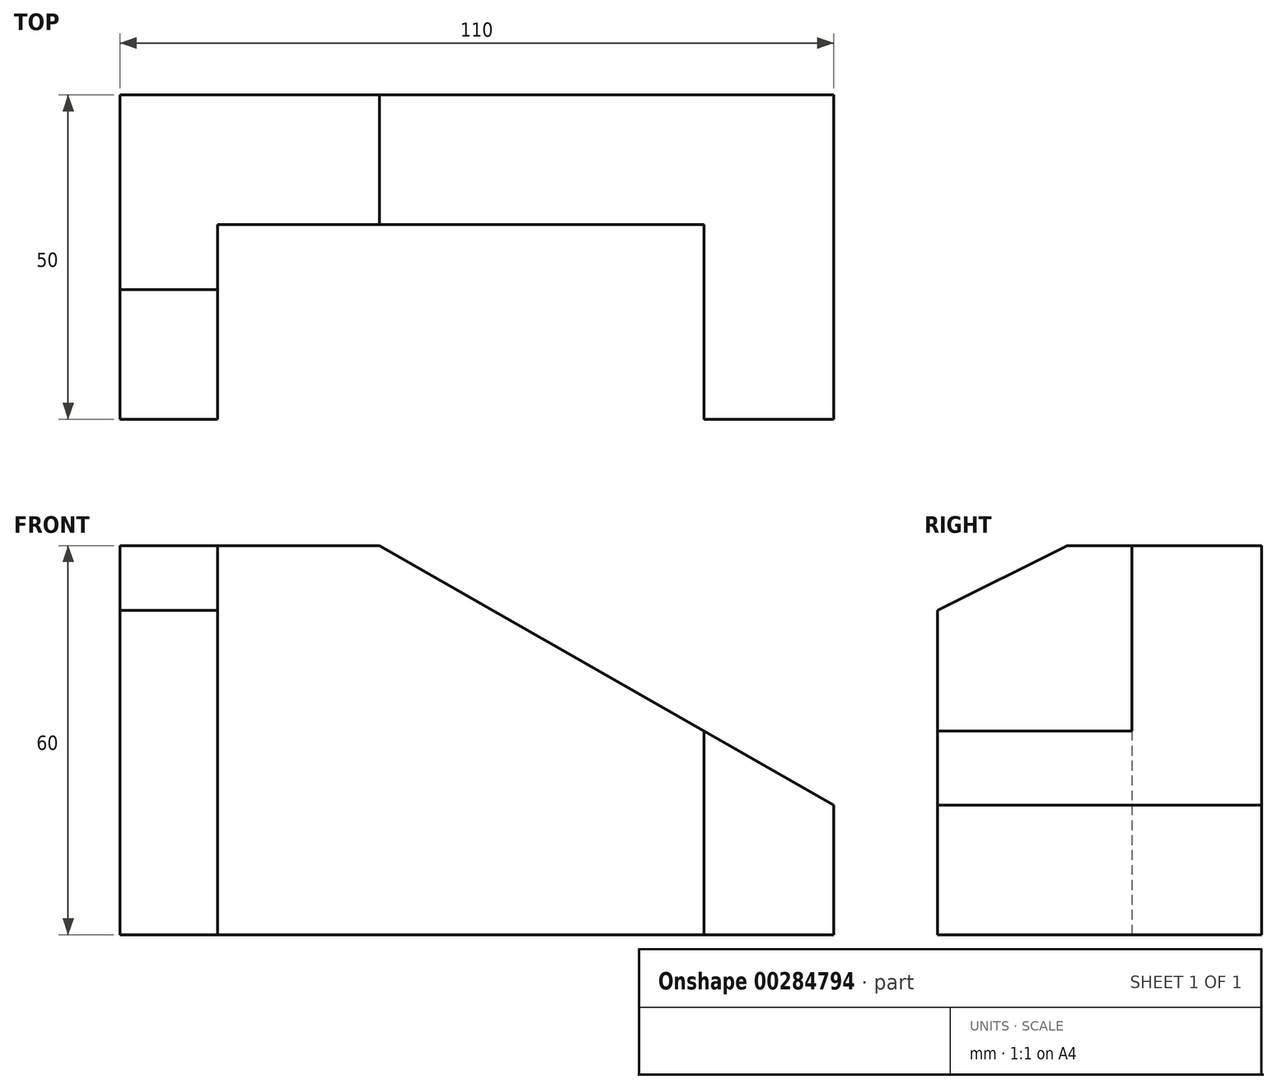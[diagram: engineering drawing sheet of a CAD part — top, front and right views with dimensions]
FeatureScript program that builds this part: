
annotation { "Feature Type Name" : "Feature", "Feature Type Description" : "" }
export const myFeature = defineFeature(function(context is Context, id is Id, definition is map)
    precondition{}
    {
        {
            var Q0;
            Q0=qCreatedBy(makeId("Top.planeOp"),FACE);
            var sketch = newSketch(context, id + "F0", { "sketchPlane" : qUnion([Q0])});
            skLineSegment(sketch, "E0.bottom", {"start": v(-55, 25) * mm, "end": v(55, 25) * mm});
            skLineSegment(sketch, "E0.top", {"start": v(-55, -25) * mm, "end": v(-40, -25) * mm});
            skLineSegment(sketch, "E0.left", {"start": v(-55, 25) * mm, "end": v(-55, -25) * mm});
            skLineSegment(sketch, "E0.right", {"start": v(55, 25) * mm, "end": v(55, -25) * mm});
            skPoint(sketch, "E0.middle", {"position": v(0, 0) * mm});
            skLineSegment(sketch, "E1.top", {"start": v(-40, 5) * mm, "end": v(35, 5) * mm});
            skLineSegment(sketch, "E1.left", {"start": v(-40, -25) * mm, "end": v(-40, 5) * mm});
            skLineSegment(sketch, "E1.right", {"start": v(35, -25) * mm, "end": v(35, 5) * mm});
            skLineSegment(sketch, "E2.trimOffspring", {"start": v(35, -25) * mm, "end": v(55, -25) * mm});
            skSolve(sketch);
        }
        {
            var Q0;
            Q0 = qSketchRegion(id + "F0", true);
            extrude(context, id + "F1", {"entities" : qUnion([Q0]), "depth" : 60 * mm});
        }
        {
            var Q0;
            Q0=makeQuery(id+"F1.opExtrude","CAP_EDGE",EDGE,{"disambiguationData":[OSD([sQuery(id+"F0.wireOp",EDGE,"E0.top")])],"isStart":false});
            chamfer(context, id + "F2", {"entities" : qUnion([Q0]), "chamferType" : ChamferType.TWO_OFFSETS, "width1" : 20 * mm, "oppositeDirection" : false, "width2" : 10 * mm, "tangentPropagation" : true});
        }
        {
            var Q0;
            Q0=makeQuery(id+"F1.opExtrude","CAP_EDGE",EDGE,{"disambiguationData":[OSD([sQuery(id+"F0.wireOp",EDGE,"E0.right")])],"isStart":false});
            chamfer(context, id + "F3", {"entities" : qUnion([Q0]), "chamferType" : ChamferType.TWO_OFFSETS, "width1" : 40 * mm, "oppositeDirection" : false, "width2" : 70 * mm, "tangentPropagation" : true});
        }
    });
